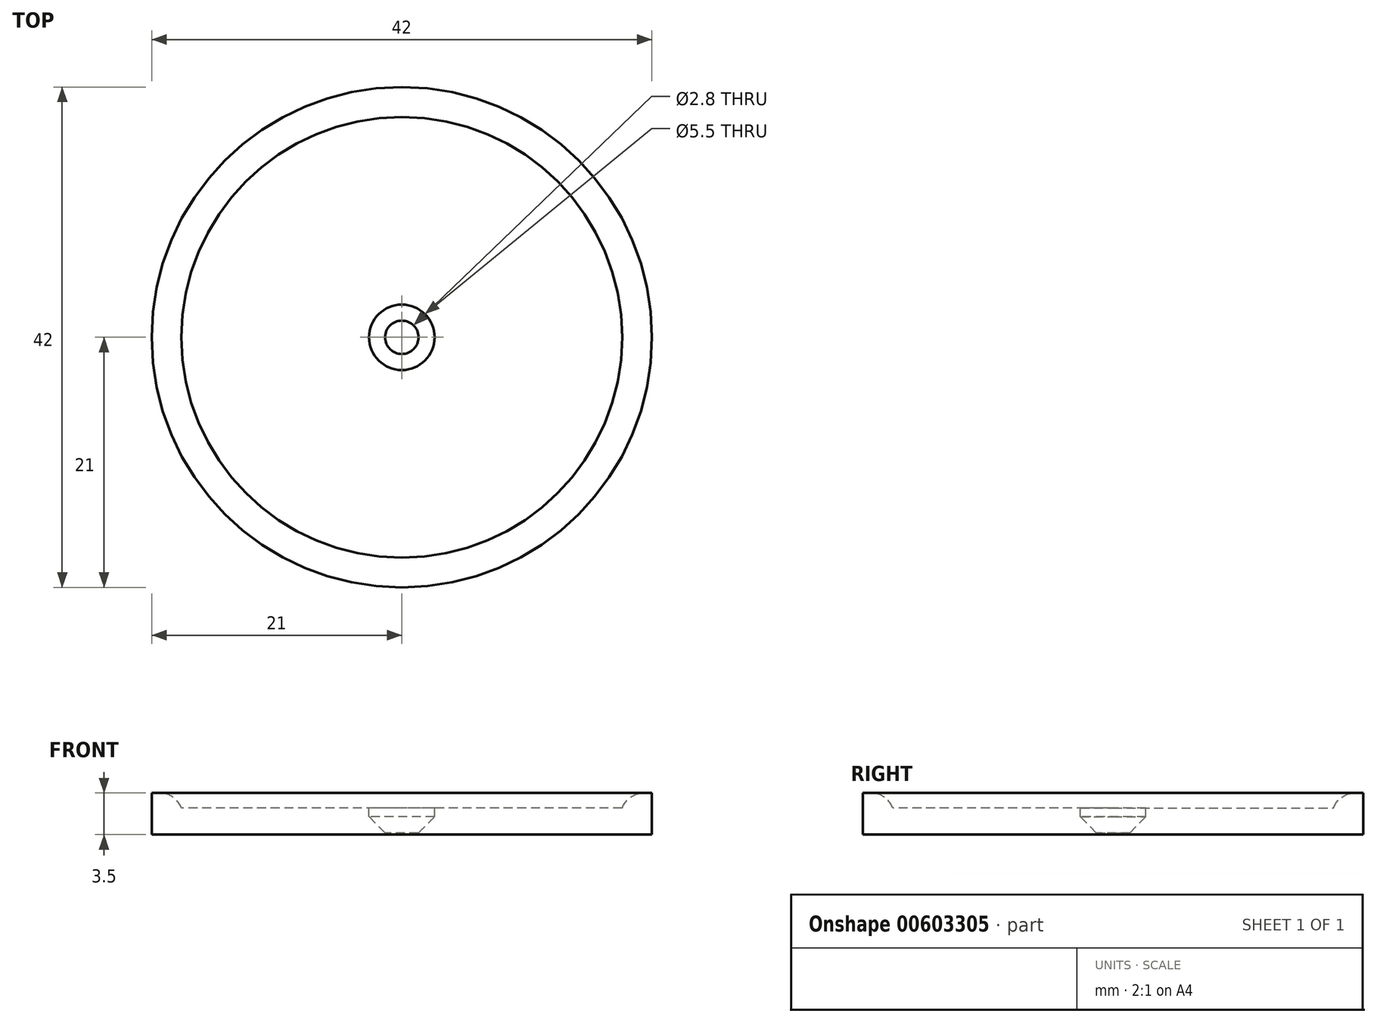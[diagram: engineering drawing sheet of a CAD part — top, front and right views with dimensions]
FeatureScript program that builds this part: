
annotation { "Feature Type Name" : "Feature", "Feature Type Description" : "" }
export const myFeature = defineFeature(function(context is Context, id is Id, definition is map)
    precondition{}
    {
        {
            var Q0;
            Q0=qCreatedBy(makeId("Top.planeOp"),FACE);
            var sketch = newSketch(context, id + "F0", { "sketchPlane" : qUnion([Q0])});
            skCircle(sketch, "E0", {"center": v(0, 0) * mm, "radius": 18.5 * mm});
            skCircle(sketch, "E1", {"center": v(0, 0) * mm, "radius": 1.4 * mm});
            skSolve(sketch);
        }
        {
            var Q0;
            Q0=qSketchRegion(id+"F0",true);
            var Q1;
            Q1 = qSketchRegion(id + "F2", true);
            extrude(context, id + "F1", {"entities" : qUnion([Q0, Q1]), "depth" : 2.25 * mm, "offsetDistance" : 25 * mm});
        }
        {
            var Q0;
            Q0=makeQuery(id+"F1.opExtrude","CAP_FACE",FACE,{"disambiguationData":[OSD([sQuery(id+"F0.wireOp",EDGE,"E0"),sQuery(id+"F0.wireOp",EDGE,"E1")])],"isStart":false});
            var sketch = newSketch(context, id + "F2", { "sketchPlane" : qUnion([Q0])});
            skCircle(sketch, "E2", {"center": v(0, 0) * mm, "radius": 2.75 * mm});
            skSolve(sketch);
        }
        {
            var Q0;
            Q0=qSketchRegion(id+"F2",true);
            extrude(context, id + "F3", {"entities" : qUnion([Q0]), "operationType" : NewBodyOperationType.REMOVE, "oppositeDirection" : true, "depth" : .1 * mm, "offsetDistance" : 25 * mm});
        }
        {
            var Q0;
            Q0=makeQuery(id+"F3.boolean.opBoolean","INTERSECT",EDGE,{"derivedFrom":[makeQuery(id+"F1.opExtrude","SWEPT_FACE",FACE,{"disambiguationData":[OSD([sQuery(id+"F0.wireOp",EDGE,"E1")])]}),makeQuery(id+"F3.opExtrude","CAP_FACE",FACE,{"disambiguationData":[OSD([sQuery(id+"F2.wireOp",EDGE,"E2")])],"isStart":false})]});
            chamfer(context, id + "F4", {"entities" : qUnion([Q0]), "width" : 2 * mm, "tangentPropagation" : true});
        }
        {
            var Q0;
            Q0=qCreatedBy(makeId("Right.planeOp"),FACE);
            var sketch = newSketch(context, id + "F5", { "sketchPlane" : qUnion([Q0])});
            skLineSegment(sketch, "E3", {"start": v(0, -33.96) * mm, "end": v(0, 48.14) * mm, "construction": true});
            skSolve(sketch);
        }
        {
            var Q0;
            Q0=qCreatedBy(makeId("Right.planeOp"),FACE);
            var sketch = newSketch(context, id + "F6", { "sketchPlane" : qUnion([Q0])});
            skLineSegment(sketch, "E4", {"start": v(-18.5, 0) * mm, "end": v(-18.5, 3.5) * mm});
            skLineSegment(sketch, "E5", {"start": v(-18.5, 3.5) * mm, "end": v(-21, 3.5) * mm});
            skLineSegment(sketch, "E6", {"start": v(-21, 3.5) * mm, "end": v(-21, 0) * mm});
            skLineSegment(sketch, "E7", {"start": v(-21, 0) * mm, "end": v(-18.5, 0) * mm});
            skSolve(sketch);
        }
        {
            var Q0;
            Q0=qSketchRegion(id+"F6",true);
            var Q1;
            Q1=sQuery(id+"F5.wireOp",EDGE,"E3");
            revolve(context, id + "F7", {"operationType" : NewBodyOperationType.ADD, "entities" : qUnion([Q0]), "axis" : qUnion([Q1]), "revolveType" : RevolveType.FULL});
        }
        {
            var Q0;
            Q0=makeQuery(id+"F7.opRevolve","SWEPT_EDGE",EDGE,{"disambiguationData":[OSD([sQuery(id+"F6.wireOp",EDGE,"E5"),sQuery(id+"F6.wireOp",EDGE,"E4")])]});
            fillet(context, id + "F8", {"entities" : qUnion([Q0]), "radius" : 2 * mm, "tangentPropagation" : true, "allowEdgeOverflow" : false});
        }
    });
